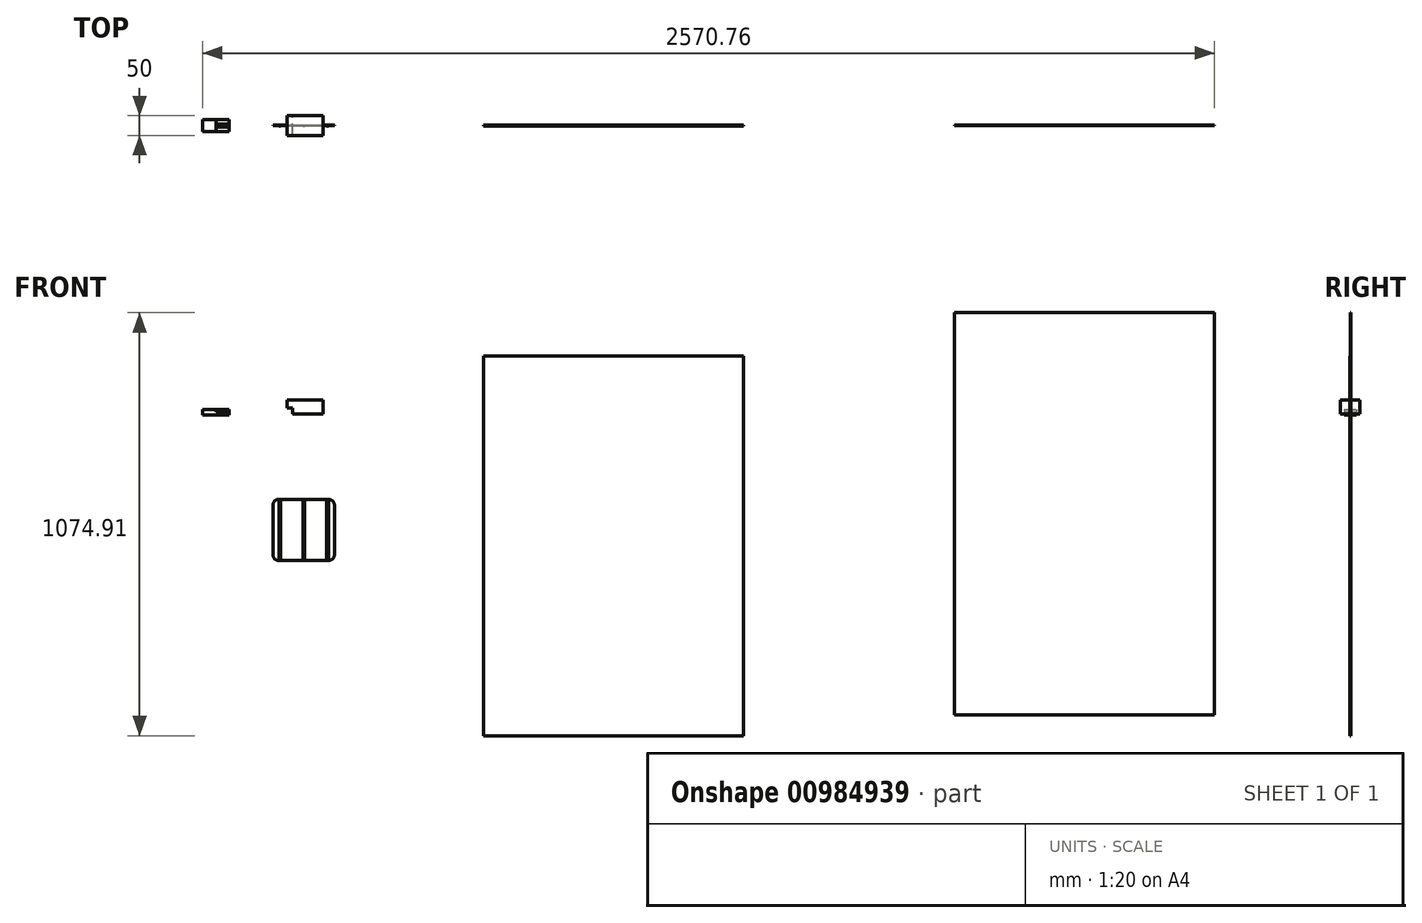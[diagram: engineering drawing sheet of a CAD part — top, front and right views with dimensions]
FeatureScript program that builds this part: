
annotation { "Feature Type Name" : "Feature", "Feature Type Description" : "" }
export const myFeature = defineFeature(function(context is Context, id is Id, definition is map)
    precondition{}
    {
        {
            var Q0;
            Q0=qCreatedBy(makeId("Front.planeOp"),FACE);
            var sketch = newSketch(context, id + "F0", { "sketchPlane" : qUnion([Q0])});
            skLineSegment(sketch, "E0", {"start": v(1286.74, 1046.2) * mm, "end": v(1947.14, 1046.2) * mm});
            skLineSegment(sketch, "E1", {"start": v(1947.14, 81) * mm, "end": v(1286.74, 81) * mm});
            skLineSegment(sketch, "E2", {"start": v(1286.74, 1046.2) * mm, "end": v(1286.74, 81) * mm});
            skLineSegment(sketch, "E3", {"start": v(1947.14, 1046.2) * mm, "end": v(1947.14, 81) * mm});
            skSolve(sketch);
        }
        {
            var Q0;
            Q0=makeQuery(id+"F0.imprint","IMPRINT",FACE,{"disambiguationData":[TD([[makeQuery(id+"F0.imprint","IMPRINT",EDGE,{"derivedFrom":sQuery(id+"F0.wireOp",EDGE,"E0")}),-1.0]])]});
            var sketch = newSketch(context, id + "F1", { "sketchPlane" : qUnion([Q0])});
            skLineSegment(sketch, "E4.bottom", {"start": v(766.3, 681.77) * mm, "end": v(892.3, 681.77) * mm});
            skLineSegment(sketch, "E4.top", {"start": v(766.3, 525.77) * mm, "end": v(892.3, 525.77) * mm});
            skLineSegment(sketch, "E4.left", {"start": v(751.3, 666.77) * mm, "end": v(751.3, 540.77) * mm});
            skLineSegment(sketch, "E4.right", {"start": v(907.3, 666.77) * mm, "end": v(907.3, 540.77) * mm});
            skPoint(sketch, "E5.visualSharp", {"position": v(751.3, 681.77) * mm});
            skArc(sketch, "E5.filletArc", {"start": v(766.3, 681.77) * mm, "mid": v(755.7, 677.38) * mm, "end": v(751.3, 666.77) * mm});
            skPoint(sketch, "E6.visualSharp", {"position": v(907.3, 681.77) * mm});
            skArc(sketch, "E6.filletArc", {"start": v(907.3, 666.77) * mm, "mid": v(902.9, 677.38) * mm, "end": v(892.3, 681.77) * mm});
            skPoint(sketch, "E7.visualSharp", {"position": v(907.3, 525.77) * mm});
            skArc(sketch, "E7.filletArc", {"start": v(892.3, 525.77) * mm, "mid": v(902.9, 530.16) * mm, "end": v(907.3, 540.77) * mm});
            skPoint(sketch, "E8.visualSharp", {"position": v(751.3, 525.77) * mm});
            skArc(sketch, "E8.filletArc", {"start": v(751.3, 540.77) * mm, "mid": v(755.7, 530.16) * mm, "end": v(766.3, 525.77) * mm});
            skLineSegment(sketch, "E9.bottom", {"start": v(3038.85, 81858.35) * mm, "end": v(2869.38, 81858.35) * mm});
            skLineSegment(sketch, "E9.top", {"start": v(3038.85, 72650.5) * mm, "end": v(2869.38, 72650.5) * mm});
            skLineSegment(sketch, "E9.left", {"start": v(3038.85, 81858.35) * mm, "end": v(3038.85, 72650.5) * mm});
            skLineSegment(sketch, "E9.right", {"start": v(2869.38, 81858.35) * mm, "end": v(2869.38, 72650.5) * mm});
            skSolve(sketch);
        }
        {
            var Q0;
            Q0=makeQuery(id+"F0.imprint","IMPRINT",FACE,{"disambiguationData":[TD([[makeQuery(id+"F0.imprint","IMPRINT",EDGE,{"derivedFrom":sQuery(id+"F0.wireOp",EDGE,"E0")}),-1.0]])]});
            extrude(context, id + "F2", {"entities" : qUnion([Q0]), "depth" : 1 * mm, "offsetDistance" : 25 * mm});
        }
        {
            var Q0;
            Q0=makeQuery(id+"F1.imprint","IMPRINT",FACE,{"disambiguationData":[TD([[makeQuery(id+"F1.imprint","IMPRINT",EDGE,{"derivedFrom":sQuery(id+"F1.wireOp",EDGE,"E4.bottom")}),-1.0]])]});
            extrude(context, id + "F3", {"entities" : qUnion([Q0]), "depth" : 1 * mm, "offsetDistance" : 25 * mm});
        }
        {
            var Q0;
            Q0=makeQuery(id+"F3.opExtrude","CAP_FACE",FACE,{"disambiguationData":[OSD([sQuery(id+"F1.wireOp",EDGE,"E4.bottom"),sQuery(id+"F1.wireOp",EDGE,"E4.top"),sQuery(id+"F1.wireOp",EDGE,"E4.left"),sQuery(id+"F1.wireOp",EDGE,"E4.right"),sQuery(id+"F1.wireOp",EDGE,"E5.filletArc"),sQuery(id+"F1.wireOp",EDGE,"E6.filletArc"),sQuery(id+"F1.wireOp",EDGE,"E7.filletArc"),sQuery(id+"F1.wireOp",EDGE,"E8.filletArc")])],"isStart":false});
            var sketch = newSketch(context, id + "F4", { "sketchPlane" : qUnion([Q0])});
            skLineSegment(sketch, "E10.bottom", {"start": v(1068.35, 691.33) * mm, "end": v(1072.64, 691.33) * mm});
            skLineSegment(sketch, "E10.top", {"start": v(1068.35, 535.33) * mm, "end": v(1072.64, 535.33) * mm});
            skLineSegment(sketch, "E10.left", {"start": v(1068.35, 691.33) * mm, "end": v(1068.35, 535.33) * mm});
            skLineSegment(sketch, "E10.right", {"start": v(1072.64, 691.33) * mm, "end": v(1072.64, 535.33) * mm});
            skLineSegment(sketch, "E11.bottom", {"start": v(1040.3, 699.13) * mm, "end": v(1044.6, 699.13) * mm});
            skLineSegment(sketch, "E11.top", {"start": v(1040.3, 543.13) * mm, "end": v(1044.6, 543.13) * mm});
            skLineSegment(sketch, "E11.left", {"start": v(1040.3, 699.13) * mm, "end": v(1040.3, 543.13) * mm});
            skLineSegment(sketch, "E11.right", {"start": v(1044.6, 699.13) * mm, "end": v(1044.6, 543.13) * mm});
            skLineSegment(sketch, "E12.bottom", {"start": v(997.94, 678.37) * mm, "end": v(1002.23, 678.37) * mm});
            skLineSegment(sketch, "E12.top", {"start": v(997.94, 522.37) * mm, "end": v(1002.23, 522.37) * mm});
            skLineSegment(sketch, "E12.left", {"start": v(997.94, 678.37) * mm, "end": v(997.94, 522.37) * mm});
            skLineSegment(sketch, "E12.right", {"start": v(1002.23, 678.37) * mm, "end": v(1002.23, 522.37) * mm});
            skSolve(sketch);
        }
        {
            var Q0;
            Q0=makeQuery(id+"F4.imprint","IMPRINT",FACE,{"disambiguationData":[TD([[makeQuery(id+"F4.imprint","IMPRINT",EDGE,{"derivedFrom":sQuery(id+"F4.wireOp",EDGE,"E10.bottom")}),-1.0]])]});
            var Q1;
            Q1=makeQuery(id+"F4.imprint","IMPRINT",FACE,{"disambiguationData":[TD([[makeQuery(id+"F4.imprint","IMPRINT",EDGE,{"derivedFrom":sQuery(id+"F4.wireOp",EDGE,"E11.bottom")}),-1.0]])]});
            var Q2;
            Q2=makeQuery(id+"F4.imprint","IMPRINT",FACE,{"disambiguationData":[TD([[makeQuery(id+"F4.imprint","IMPRINT",EDGE,{"derivedFrom":sQuery(id+"F4.wireOp",EDGE,"E12.bottom")}),-1.0]])]});
            extrude(context, id + "F5", {"entities" : qUnion([Q0, Q1, Q2]), "depth" : 0.5 * mm, "offsetDistance" : 25 * mm});
        }
        {
            var Q0;
            Q0=makeQuery(id+"F5.opExtrude","SWEPT_BODY",BODY,{"disambiguationData":[OSD([sQuery(id+"F4.wireOp",EDGE,"E12.bottom"),sQuery(id+"F4.wireOp",EDGE,"E12.top"),sQuery(id+"F4.wireOp",EDGE,"E12.left"),sQuery(id+"F4.wireOp",EDGE,"E12.right")])]});
            transform(context, id + "F6", {"entities" : qUnion([Q0]), "transformType" : TransformType.TRANSLATION_3D, "dx" : -232.8 * mm, "dy" : 0 * mm, "dz" : 3.3 * mm, "makeCopy" : false});
        }
        {
            var Q0;
            Q0=makeQuery(id+"F5.opExtrude","SWEPT_BODY",BODY,{"disambiguationData":[OSD([sQuery(id+"F4.wireOp",EDGE,"E12.bottom"),sQuery(id+"F4.wireOp",EDGE,"E12.top"),sQuery(id+"F4.wireOp",EDGE,"E12.left"),sQuery(id+"F4.wireOp",EDGE,"E12.right")])]});
            transform(context, id + "F7", {"entities" : qUnion([Q0]), "transformType" : TransformType.TRANSLATION_3D, "dx" : 6E-4000 * mm, "dy" : 0 * mm, "dz" : 0 * mm, "makeCopy" : false});
        }
        {
            var Q0;
            Q0=makeQuery(id+"F5.opExtrude","SWEPT_BODY",BODY,{"disambiguationData":[OSD([sQuery(id+"F4.wireOp",EDGE,"E12.bottom"),sQuery(id+"F4.wireOp",EDGE,"E12.top"),sQuery(id+"F4.wireOp",EDGE,"E12.left"),sQuery(id+"F4.wireOp",EDGE,"E12.right")])]});
            var Q1;
            Q1=makeQuery(id+"F5.opExtrude","CAP_VERTEX",VERTEX,{"disambiguationData":[OSD([sQuery(id+"F4.wireOp",EDGE,"E12.top"),sQuery(id+"F4.wireOp",EDGE,"E12.left")])],"isStart":false});
            var Q2;
            Q2=makeQuery(id+"F3.opExtrude","CAP_EDGE",EDGE,{"disambiguationData":[OSD([sQuery(id+"F1.wireOp",EDGE,"E4.top")])],"isStart":false});
            transform(context, id + "F8", {"entities" : qUnion([Q0]), "transformType" : TransformType.TRANSLATION_ENTITY, "oppositeDirectionEntity" : false, "transformLine" : qUnion([Q1, Q2]), "makeCopy" : false});
        }
        {
            var Q0;
            Q0=makeQuery(id+"F5.opExtrude","SWEPT_BODY",BODY,{"disambiguationData":[OSD([sQuery(id+"F4.wireOp",EDGE,"E12.bottom"),sQuery(id+"F4.wireOp",EDGE,"E12.top"),sQuery(id+"F4.wireOp",EDGE,"E12.left"),sQuery(id+"F4.wireOp",EDGE,"E12.right")])]});
            var Q1;
            Q1=makeQuery(id+"F5.opExtrude","CAP_VERTEX",VERTEX,{"disambiguationData":[OSD([sQuery(id+"F4.wireOp",EDGE,"E12.bottom"),sQuery(id+"F4.wireOp",EDGE,"E12.right")])],"isStart":true});
            var Q2;
            Q2=makeQuery(id+"F3.opExtrude","CAP_VERTEX",VERTEX,{"disambiguationData":[OSD([sQuery(id+"F1.wireOp",EDGE,"E4.bottom"),sQuery(id+"F1.wireOp",EDGE,"E6.filletArc")])],"isStart":false});
            transform(context, id + "F9", {"entities" : qUnion([Q0]), "transformType" : TransformType.TRANSLATION_ENTITY, "oppositeDirectionEntity" : false, "transformLine" : qUnion([Q1, Q2]), "makeCopy" : false});
        }
        {
            var Q0;
            Q0=makeQuery(id+"F5.opExtrude","SWEPT_BODY",BODY,{"disambiguationData":[OSD([sQuery(id+"F4.wireOp",EDGE,"E11.bottom"),sQuery(id+"F4.wireOp",EDGE,"E11.top"),sQuery(id+"F4.wireOp",EDGE,"E11.left"),sQuery(id+"F4.wireOp",EDGE,"E11.right")])]});
            var Q1;
            Q1=sQuery(id+"F4.wireOp",VERTEX,"E11.bottom.start");
            var Q2;
            Q2=makeQuery(id+"F3.opExtrude","CAP_VERTEX",VERTEX,{"disambiguationData":[OSD([sQuery(id+"F1.wireOp",EDGE,"E4.bottom"),sQuery(id+"F1.wireOp",EDGE,"E5.filletArc")])],"isStart":false});
            transform(context, id + "F10", {"entities" : qUnion([Q0]), "transformType" : TransformType.TRANSLATION_ENTITY, "oppositeDirectionEntity" : false, "transformLine" : qUnion([Q1, Q2]), "makeCopy" : false});
        }
        {
            var Q0;
            Q0=sQuery(id+"F4.wireOp",EDGE,"E10.bottom");
            cPoint(context, id + "F11", {"entities" : qUnion([Q0]), "parameter" : 0.5});
        }
        {
            var Q0;
            Q0=makeQuery(id+"F3.opExtrude","CAP_EDGE",EDGE,{"disambiguationData":[OSD([sQuery(id+"F1.wireOp",EDGE,"E4.bottom")])],"isStart":false});
            cPoint(context, id + "F12", {"entities" : qUnion([Q0]), "parameter" : 0.5});
        }
        {
            var Q0;
            Q0=makeQuery(id+"F5.opExtrude","SWEPT_BODY",BODY,{"disambiguationData":[OSD([sQuery(id+"F4.wireOp",EDGE,"E10.bottom"),sQuery(id+"F4.wireOp",EDGE,"E10.top"),sQuery(id+"F4.wireOp",EDGE,"E10.left"),sQuery(id+"F4.wireOp",EDGE,"E10.right")])]});
            var Q1;
            Q1=qCreatedBy(id+"F11",VERTEX);
            var Q2;
            Q2=qCreatedBy(id+"F12",VERTEX);
            transform(context, id + "F13", {"entities" : qUnion([Q0]), "transformType" : TransformType.TRANSLATION_ENTITY, "oppositeDirectionEntity" : false, "transformLine" : qUnion([Q1, Q2]), "makeCopy" : false});
        }
        {
            var Q0;
            Q0=makeQuery(id+"F2.opExtrude","CAP_FACE",FACE,{"disambiguationData":[OSD([sQuery(id+"F0.wireOp",EDGE,"E0"),sQuery(id+"F0.wireOp",EDGE,"E1"),sQuery(id+"F0.wireOp",EDGE,"E2"),sQuery(id+"F0.wireOp",EDGE,"E3")])],"isStart":false});
            var sketch = newSketch(context, id + "F14", { "sketchPlane" : qUnion([Q0])});
            skLineSegment(sketch, "E13.bottom", {"start": v(801.5, 913.01) * mm, "end": v(878.96, 913.01) * mm});
            skLineSegment(sketch, "E13.top", {"start": v(801.5, 898.01) * mm, "end": v(878.96, 898.01) * mm});
            skLineSegment(sketch, "E13.left", {"start": v(801.5, 913.01) * mm, "end": v(801.5, 898.01) * mm});
            skLineSegment(sketch, "E13.right", {"start": v(878.96, 913.01) * mm, "end": v(878.96, 898.01) * mm});
            skLineSegment(sketch, "E14.bottom", {"start": v(878.96, 913.01) * mm, "end": v(787.59, 913.01) * mm});
            skLineSegment(sketch, "E14.top", {"start": v(878.96, 934.06) * mm, "end": v(787.59, 934.06) * mm});
            skLineSegment(sketch, "E14.left", {"start": v(878.96, 913.01) * mm, "end": v(878.96, 934.06) * mm});
            skLineSegment(sketch, "E14.right", {"start": v(787.59, 913.01) * mm, "end": v(787.59, 934.06) * mm});
            skLineSegment(sketch, "E15.bottom", {"start": v(787.59, 926.24) * mm, "end": v(765.52, 926.24) * mm});
            skLineSegment(sketch, "E15.top", {"start": v(787.59, 912.98) * mm, "end": v(765.52, 912.98) * mm});
            skLineSegment(sketch, "E15.left", {"start": v(787.59, 923.54) * mm, "end": v(787.59, 912.98) * mm});
            skLineSegment(sketch, "E15.right", {"start": v(765.52, 926.24) * mm, "end": v(765.52, 912.98) * mm});
            skSolve(sketch);
        }
        {
            var Q0;
            {var subQ1=sQuery(id+"F14.wireOp",EDGE,"E14.top");Q0=makeQuery(id+"F14.imprint","IMPRINT",FACE,{"disambiguationData":[TD([[makeQuery(id+"F14.imprint","IMPRINT",EDGE,{"derivedFrom":subQ1}),1.0]])]});}
            var sketch = newSketch(context, id + "F15", { "sketchPlane" : qUnion([Q0])});
            skLineSegment(sketch, "E16.bottom", {"start": v(-15.18, -3.1) * mm, "end": v(62.27, -3.1) * mm});
            skLineSegment(sketch, "E16.top", {"start": v(-15.18, -18.1) * mm, "end": v(62.27, -18.1) * mm});
            skLineSegment(sketch, "E16.left", {"start": v(-15.18, -3.1) * mm, "end": v(-15.18, -18.1) * mm});
            skLineSegment(sketch, "E16.right", {"start": v(62.27, -3.1) * mm, "end": v(62.27, -18.1) * mm});
            skLineSegment(sketch, "E17.bottom", {"start": v(62.27, -3.1) * mm, "end": v(-29.1, -3.1) * mm});
            skLineSegment(sketch, "E17.top", {"start": v(62.27, 17.96) * mm, "end": v(-29.1, 17.96) * mm});
            skLineSegment(sketch, "E17.left", {"start": v(62.27, -3.1) * mm, "end": v(62.27, 17.96) * mm});
            skLineSegment(sketch, "E17.right", {"start": v(-29.1, -3.1) * mm, "end": v(-29.1, 17.96) * mm});
            skLineSegment(sketch, "E18.bottom", {"start": v(-29.1, 10.13) * mm, "end": v(-51.17, 10.13) * mm});
            skLineSegment(sketch, "E18.top", {"start": v(-29.1, -3.13) * mm, "end": v(-51.17, -3.13) * mm});
            skLineSegment(sketch, "E18.left", {"start": v(-29.1, 7.43) * mm, "end": v(-29.1, -3.13) * mm});
            skLineSegment(sketch, "E18.right", {"start": v(-51.17, 10.13) * mm, "end": v(-51.17, -3.13) * mm});
            skLineSegment(sketch, "E19.top", {"start": v(572.41, 895.67) * mm, "end": v(640.41, 895.67) * mm});
            skLineSegment(sketch, "E19.left", {"start": v(572.41, 910.17) * mm, "end": v(572.41, 895.67) * mm});
            skLineSegment(sketch, "E20.bottom", {"start": v(572.41, 910.17) * mm, "end": v(606.41, 910.17) * mm});
            skLineSegment(sketch, "E20.top", {"start": v(572.41, 895.67) * mm, "end": v(606.41, 895.67) * mm});
            skLineSegment(sketch, "E20.right", {"start": v(606.41, 910.17) * mm, "end": v(606.41, 895.67) * mm});
            skLineSegment(sketch, "E21", {"start": v(606.41, 902.92) * mm, "end": v(640.41, 902.92) * mm});
            skLineSegment(sketch, "E22.top", {"start": v(606.41, 906.59) * mm, "end": v(640.41, 906.59) * mm});
            skLineSegment(sketch, "E22.left", {"start": v(606.41, 902.92) * mm, "end": v(606.41, 906.59) * mm});
            skLineSegment(sketch, "E22.right", {"start": v(640.41, 902.92) * mm, "end": v(640.41, 906.59) * mm});
            skLineSegment(sketch, "E23", {"start": v(640.41, 902.92) * mm, "end": v(640.41, 895.67) * mm});
            skSolve(sketch);
        }
        {
            var Q0;
            {var subQ3=sQuery(id+"F15.wireOp",EDGE,"fItkzUZf-nGmU-rPvr-P6rd-NpfCkkb8rq9y.bottom");Q0=makeQuery(id+"F15.imprint","IMPRINT",FACE,{"disambiguationData":[TD([[makeQuery(id+"F15.imprint","IMPRINT",EDGE,{"derivedFrom":subQ3}),-1.0]])]});}
            var Q1;
            Q1=makeQuery(id+"F15.imprint","IMPRINT",FACE,{"disambiguationData":[TD([[makeQuery(id+"F15.imprint","IMPRINT",EDGE,{"derivedFrom":sQuery(id+"F15.wireOp",EDGE,"4efb6f42-2137-4167-9bb1-179bed798946.left")}),-1.0]])]});
            var Q2;
            {var subQ1=sQuery(id+"F14.wireOp",EDGE,"E14.top");Q2=makeQuery(id+"F14.imprint","IMPRINT",FACE,{"disambiguationData":[TD([[makeQuery(id+"F14.imprint","IMPRINT",EDGE,{"derivedFrom":subQ1}),1.0]])]});}
            var Q3;
            Q3=makeQuery(id+"F14.imprint","IMPRINT",FACE,{"disambiguationData":[TD([[makeQuery(id+"F14.imprint","IMPRINT",EDGE,{"derivedFrom":sQuery(id+"F14.wireOp",EDGE,"E13.top")}),1.0]])]});
            extrude(context, id + "F16", {"entities" : qUnion([Q0, Q1, Q2, Q3]), "endBound" : BoundingType.SYMMETRIC, "depth" : 50 * mm, "offsetDistance" : 25 * mm});
        }
        {
            var Q0;
            {var subQ1=sQuery(id+"F15.wireOp",EDGE,"E20.bottom");Q0=makeQuery(id+"F15.imprint","IMPRINT",FACE,{"disambiguationData":[TD([[makeQuery(id+"F15.imprint","IMPRINT",EDGE,{"derivedFrom":subQ1}),-1.0]])]});}
            var Q1;
            {var subQ0=sQuery(id+"F15.wireOp",EDGE,"E19.top");Q1=makeQuery(id+"F15.imprint","IMPRINT",FACE,{"disambiguationData":[TD([[makeQuery(id+"F15.imprint","IMPRINT",EDGE,{"derivedFrom":subQ0}),1.0]])]});}
            extrude(context, id + "F17", {"entities" : qUnion([Q0, Q1]), "endBound" : BoundingType.SYMMETRIC, "depth" : 31 * mm, "offsetDistance" : 25 * mm});
        }
        {
            var Q0;
            Q0=makeQuery(id+"F15.imprint","IMPRINT",FACE,{"disambiguationData":[TD([[makeQuery(id+"F15.imprint","IMPRINT",EDGE,{"derivedFrom":sQuery(id+"F15.wireOp",EDGE,"E21")}),1.0]])]});
            var Q1;
            Q1=sQuery(id+"F15.wireOp",EDGE,"E22.top");
            revolve(context, id + "F18", {"surfaceOperationType" : NewSurfaceOperationType.NEW, "entities" : qUnion([Q0]), "axis" : qUnion([Q1]), "revolveType" : RevolveType.FULL});
        }
        {
            var Q0;
            Q0=makeQuery(id+"F14.imprint","IMPRINT",FACE,{"disambiguationData":[TD([[makeQuery(id+"F14.imprint","IMPRINT",EDGE,{"derivedFrom":makeQuery(id+"F2.opExtrude","CAP_EDGE",EDGE,{"disambiguationData":[OSD([sQuery(id+"F0.wireOp",EDGE,"E0")])],"isStart":false})}),-1.0]])]});
            extrude(context, id + "F19", {"entities" : qUnion([Q0]), "depth" : 1 * mm, "offsetDistance" : 25.4 * mm});
        }
        {
            var Q0;
            Q0=qCreatedBy(makeId("Front.planeOp"),FACE);
            var sketch = newSketch(context, id + "F20", { "sketchPlane" : qUnion([Q0])});
            skLineSegment(sketch, "E24.bottom", {"start": v(2482.77, 1155.9) * mm, "end": v(3143.17, 1155.9) * mm});
            skLineSegment(sketch, "E24.top", {"start": v(2482.77, 133.56) * mm, "end": v(3143.17, 133.56) * mm});
            skLineSegment(sketch, "E24.left", {"start": v(2482.77, 1155.9) * mm, "end": v(2482.77, 133.56) * mm});
            skLineSegment(sketch, "E24.right", {"start": v(3143.17, 1155.9) * mm, "end": v(3143.17, 133.56) * mm});
            skSolve(sketch);
        }
        {
            var Q0;
            Q0=makeQuery(id+"F20.imprint","IMPRINT",FACE,{"disambiguationData":[TD([[makeQuery(id+"F20.imprint","IMPRINT",EDGE,{"derivedFrom":sQuery(id+"F20.wireOp",EDGE,"E24.bottom")}),-1.0]])]});
            extrude(context, id + "F21", {"entities" : qUnion([Q0]), "depth" : 1 * mm, "offsetDistance" : 25.4 * mm});
        }
    });
